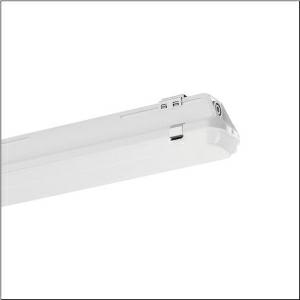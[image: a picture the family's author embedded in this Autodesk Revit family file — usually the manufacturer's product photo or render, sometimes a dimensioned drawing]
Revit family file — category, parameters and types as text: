
# Revit family: monsun_r__11_51fp10dp4b0u_db1a
name_source: partatom
category: Lighting Fixtures
units: mm (PartAtom-declared; Revit-internal decimal feet)

## family parameters
Cut with Voids When Loaded = No
Host = Face
Light Source = No
Part Type = Normal
Room Calculation Point = No
Round Connector Dimension = Use Diameter
Shared = No

## types (1)
- --- (1 x LED, 12110 lm, 63.7 W, 4000K)
    Apparent Load = 64 VA
    CIE Flux Codes = 47 76 93 94 100
    Color Rendering = 80
    Color Temperature = 4000K
    Default Elevation = 1800 mm
    Description = Monsun® 11, damp-proof luminaire, chain hanger, primary optical cover: enclosure, of PMMA, light emission: direct distribution, primary light characteristic: symmetric, installation type: suspended mounting, surface-mounted, horizontal mounting, vertical mounting, LED, rated luminous flux: 12.110lm, luminous efficacy: 190lm/W, light colour: 840, colour temperature: 4000K, control gear: DALI 2, with terminal, 5-pole, max. 2.5mm², mains connection: 220..240V, AC, 50/60Hz, rated input power: 64W, luminaire housing, of glass-fibre reinforced polyester, uncoated, bright grey, incl. chain hanger, length: 1.590mm, width: 90mm, height: 88mm, clip for enclosure, of stainless steel (V2A), ceiling mounting element, of stainless steel (V2A), chain hanger, of stainless steel (V2A), protection rating (complete): IP66, insulation class (complete): insulation class I (protective earthing), certification: CE, ENEC, VDE, UKCA, protection symbol: D, impact resistance: IK04, permissible operating ambient temperature: -40..+35°C, standard: EN 50419, EN 60598-2-1, contact your sales advisor before using the luminaires in applications with unclear chemical exposure, large temperature fluctuations or condensation-forming humidity, LABS conformity tested according to VDMA 24364:2018-05, no direct snow, no direct sun, no direct rain, for indoor or canopied outdoor use, corresponds to IFS (International Featured Standards) requirements for safety and quality in the food industry, packaging unit: 1 piece
    Height = 89 mm
    Lamp = 1 x LED
    Lamp Light Flux = 12110 lm
    Lamp Power = 63.7 W
    Lamp count = 1
    Length = 1590 mm
    Luminous efficacy = 190 lm/W
    Manufacturer = Siteco
    ModVariant = No
    Model = 51FP10DP4B0U
    Mounting Place = Ceiling
    Mounting Type = Surface mounted
    Number of Poles = 1
    OnlyDefault = Yes
    Power Factor = 1
    Product Name = Monsun® 11
    Product group = damp-proof luminaire
    ProductGroupID = 300
    Protection Class = Protection class I
    Protection Degree = IP 66
    RLX_Detail_Level = 1
    RLX_Emergency_Light_Flux = 0 lm
    RLX_Emergency_Type = 0
    RLX_Emergency_Type_DB = No
    RlxData = <blob elided: 92481 chars, md5=abd1b60d>
    Socket = socket
    Standby Power = 0 W
    System Light Flux = 12110 lm
    System Power = 64 W
    Type Comments = factory setting: luminous flux: 100 % | dim-lin: 254 | 441 mA
    Type Image = l_1349237.jpg
    URL = http://relux.com
    VarID = @adj_023160
    Voltage = 0 V
    Weight = 0.00 kg
    Width = 90 mm

## geometry (parser evidence)
native form markers: Blend x4, Sweep x13
no freeform markers — native parametric forms only
